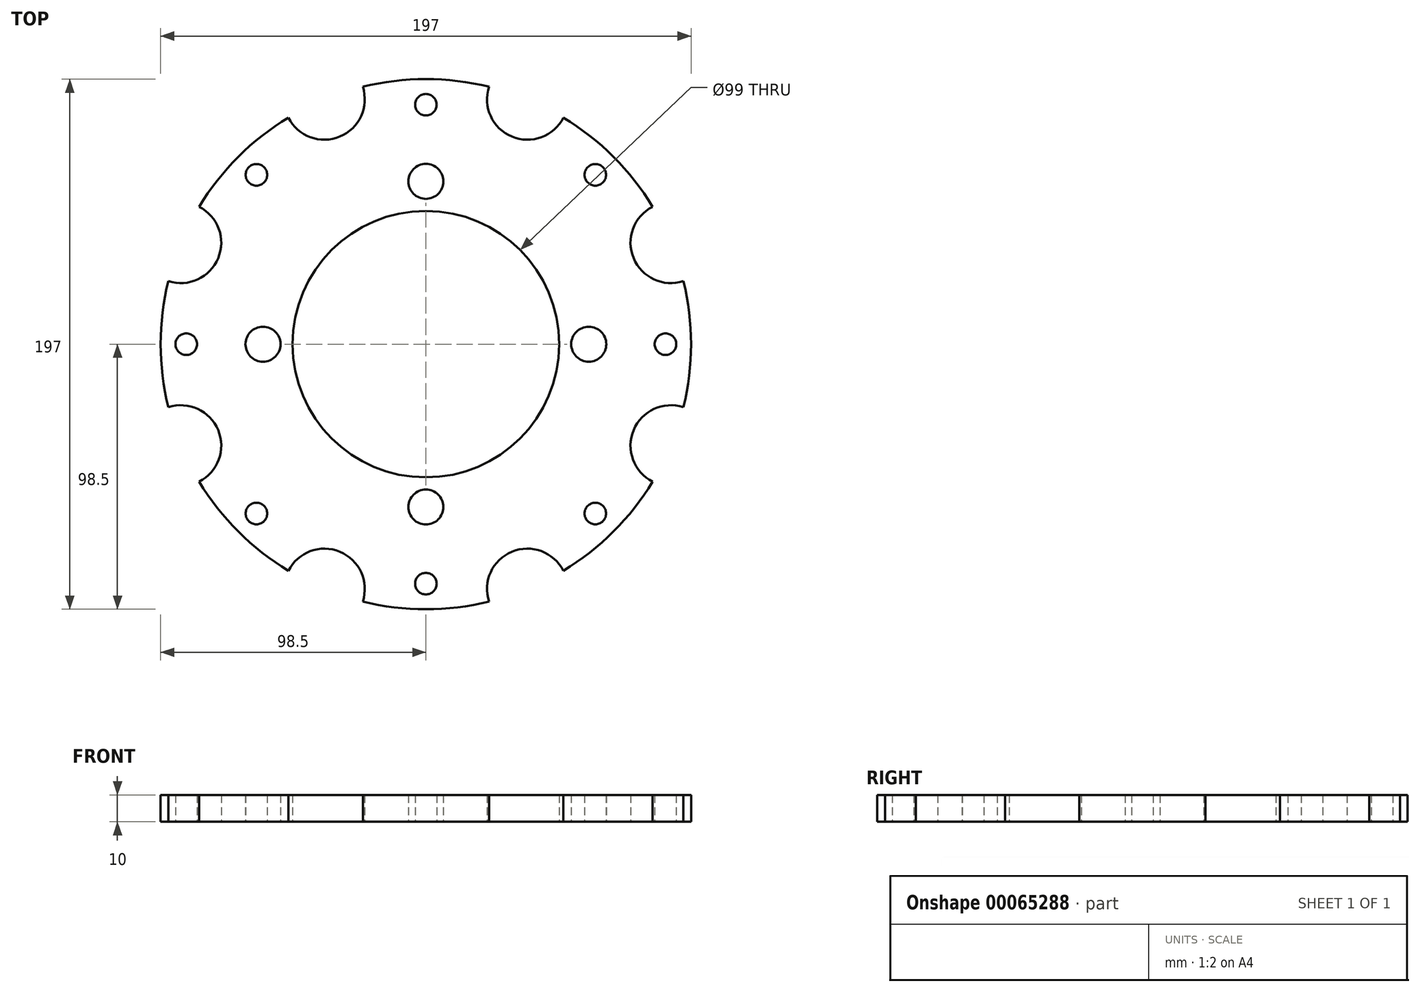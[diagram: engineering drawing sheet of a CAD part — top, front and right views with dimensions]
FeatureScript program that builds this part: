
annotation { "Feature Type Name" : "Feature", "Feature Type Description" : "" }
export const myFeature = defineFeature(function(context is Context, id is Id, definition is map)
    precondition{}
    {
        {
            var Q0;
            Q0=qCreatedBy(makeId("Top.planeOp"),FACE);
            var sketch = newSketch(context, id + "F0", { "sketchPlane" : qUnion([Q0])});
            skArc(sketch, "E0", {"start": v(98.5, 0) * mm, "mid": v(97.8, 11.8) * mm, "end": v(95.67, 23.44) * mm});
            skArc(sketch, "E1", {"start": v(-76, 37.7) * mm, "mid": v(-78.22, 45.55) * mm, "end": v(-84.22, 51.08) * mm});
            skArc(sketch, "E2", {"start": v(-22.7, 91) * mm, "mid": v(-22.88, 93.37) * mm, "end": v(-23.44, 95.67) * mm});
            skArc(sketch, "E3", {"start": v(-22.7, -91) * mm, "mid": v(-34.2, -76.41) * mm, "end": v(-51.08, -84.22) * mm});
            skArc(sketch, "E4", {"start": v(-76, -37.7) * mm, "mid": v(-82.2, -25.55) * mm, "end": v(-95.67, -23.44) * mm});
            skArc(sketch, "E5", {"start": v(-95.67, 23.44) * mm, "mid": v(-82.2, 25.55) * mm, "end": v(-76, 37.7) * mm});
            skArc(sketch, "E6", {"start": v(-95.67, 23.44) * mm, "mid": v(-98.5, 0) * mm, "end": v(-95.67, -23.44) * mm});
            skArc(sketch, "E7", {"start": v(-51.08, 84.22) * mm, "mid": v(-34.2, 76.41) * mm, "end": v(-22.7, 91) * mm});
            skArc(sketch, "E8", {"start": v(-51.08, 84.22) * mm, "mid": v(-69.65, 69.65) * mm, "end": v(-84.22, 51.08) * mm});
            skArc(sketch, "E9", {"start": v(23.44, 95.67) * mm, "mid": v(31.95, 77.14) * mm, "end": v(51.08, 84.22) * mm});
            skArc(sketch, "E10", {"start": v(23.44, 95.67) * mm, "mid": v(0, 98.5) * mm, "end": v(-23.44, 95.67) * mm});
            skArc(sketch, "E11", {"start": v(84.22, 51.08) * mm, "mid": v(77.14, 31.95) * mm, "end": v(95.67, 23.44) * mm});
            skArc(sketch, "E12", {"start": v(84.22, 51.08) * mm, "mid": v(69.65, 69.65) * mm, "end": v(51.08, 84.22) * mm});
            skArc(sketch, "E13", {"start": v(95.67, -23.44) * mm, "mid": v(77.14, -31.95) * mm, "end": v(84.22, -51.08) * mm});
            skArc(sketch, "E14", {"start": v(95.67, -23.44) * mm, "mid": v(97.8, -11.8) * mm, "end": v(98.5, 0) * mm});
            skArc(sketch, "E15", {"start": v(51.08, -84.22) * mm, "mid": v(31.95, -77.14) * mm, "end": v(23.44, -95.67) * mm});
            skArc(sketch, "E16", {"start": v(51.08, -84.22) * mm, "mid": v(69.65, -69.65) * mm, "end": v(84.22, -51.08) * mm});
            skArc(sketch, "E17", {"start": v(-23.44, -95.67) * mm, "mid": v(-22.88, -93.37) * mm, "end": v(-22.7, -91) * mm});
            skArc(sketch, "E18", {"start": v(-23.44, -95.67) * mm, "mid": v(0, -98.5) * mm, "end": v(23.44, -95.67) * mm});
            skArc(sketch, "E19", {"start": v(-84.22, -51.08) * mm, "mid": v(-78.22, -45.55) * mm, "end": v(-76, -37.7) * mm});
            skArc(sketch, "E20", {"start": v(-84.22, -51.08) * mm, "mid": v(-69.65, -69.65) * mm, "end": v(-51.08, -84.22) * mm});
            skCircle(sketch, "E21", {"center": v(0, 0) * mm, "radius": 49.5 * mm});
            skCircle(sketch, "E22", {"center": v(60.5, 0) * mm, "radius": 6.5 * mm});
            skCircle(sketch, "E23", {"center": v(0, 60.5) * mm, "radius": 6.5 * mm});
            skCircle(sketch, "E24", {"center": v(-60.5, 0) * mm, "radius": 6.5 * mm});
            skCircle(sketch, "E25", {"center": v(0, -60.5) * mm, "radius": 6.5 * mm});
            skCircle(sketch, "E26", {"center": v(89, 0) * mm, "radius": 4 * mm});
            skCircle(sketch, "E27", {"center": v(62.93, 62.93) * mm, "radius": 4 * mm});
            skCircle(sketch, "E28", {"center": v(0, 89) * mm, "radius": 4 * mm});
            skCircle(sketch, "E29", {"center": v(-62.93, 62.93) * mm, "radius": 4 * mm});
            skCircle(sketch, "E30", {"center": v(-89, 0) * mm, "radius": 4 * mm});
            skCircle(sketch, "E31", {"center": v(-62.93, -62.93) * mm, "radius": 4 * mm});
            skCircle(sketch, "E32", {"center": v(0, -89) * mm, "radius": 4 * mm});
            skCircle(sketch, "E33", {"center": v(62.93, -62.93) * mm, "radius": 4 * mm});
            skSolve(sketch);
        }
        {
            var Q0;
            Q0=makeQuery(id+"F0.imprint","IMPRINT",FACE,{"disambiguationData":[TD([[makeQuery(id+"F0.imprint","IMPRINT",EDGE,{"derivedFrom":sQuery(id+"F0.wireOp",EDGE,"E0")}),1.0]])]});
            extrude(context, id + "F1", {"entities" : qUnion([Q0]), "depth" : 10 * mm, "offsetDistance" : 25 * mm});
        }
    });
